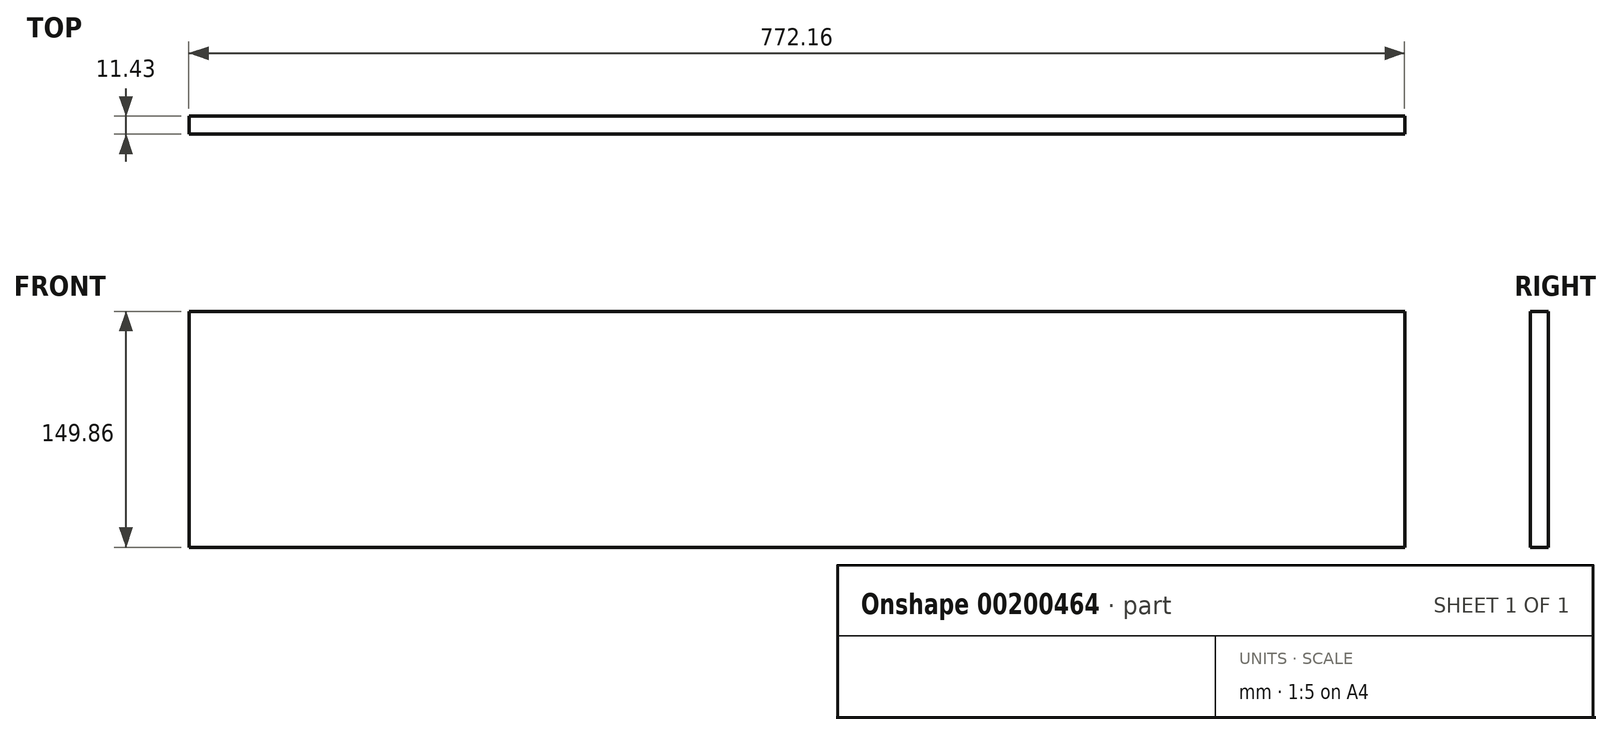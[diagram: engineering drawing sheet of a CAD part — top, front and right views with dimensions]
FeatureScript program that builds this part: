
annotation { "Feature Type Name" : "Feature", "Feature Type Description" : "" }
export const myFeature = defineFeature(function(context is Context, id is Id, definition is map)
    precondition{}
    {
        {
            var Q0;
            Q0=qCreatedBy(makeId("Front.planeOp"),FACE);
            var sketch = newSketch(context, id + "F0", { "sketchPlane" : qUnion([Q0])});
            skLineSegment(sketch, "E0.bottom", {"start": v(-1056.9, -12.67) * mm, "end": v(-284.75, -12.67) * mm});
            skLineSegment(sketch, "E0.top", {"start": v(-1056.9, -162.53) * mm, "end": v(-284.75, -162.53) * mm});
            skLineSegment(sketch, "E0.left", {"start": v(-1056.9, -12.67) * mm, "end": v(-1056.9, -162.53) * mm});
            skLineSegment(sketch, "E0.right", {"start": v(-284.75, -12.67) * mm, "end": v(-284.75, -162.53) * mm});
            skSolve(sketch);
        }
        {
            var Q0;
            Q0 = qSketchRegion(id + "F0", true);
            extrude(context, id + "F1", {"entities" : qUnion([Q0]), "depth" : 11.43 * mm});
        }
    });
